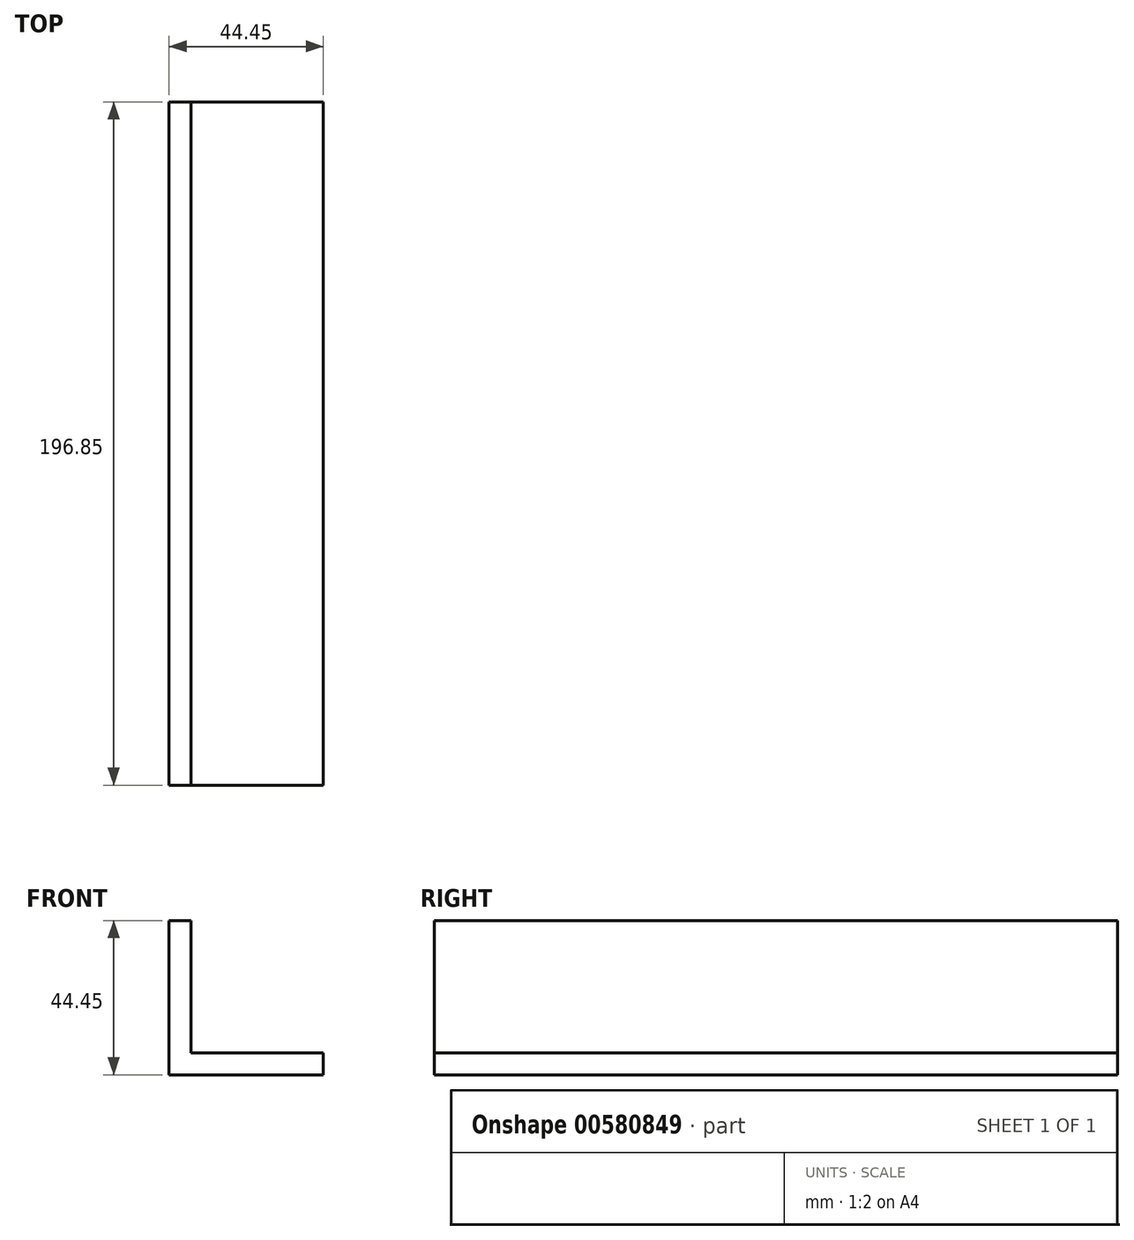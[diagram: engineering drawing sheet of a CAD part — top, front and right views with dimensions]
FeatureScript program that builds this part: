
annotation { "Feature Type Name" : "Feature", "Feature Type Description" : "" }
export const myFeature = defineFeature(function(context is Context, id is Id, definition is map)
    precondition{}
    {
        {
            var Q0;
            Q0=qCreatedBy(makeId("Front.planeOp"),FACE);
            var sketch = newSketch(context, id + "F0", { "sketchPlane" : qUnion([Q0])});
            skLineSegment(sketch, "E0.bottom", {"start": v(-23.34, 19.35) * mm, "end": v(-16.99, 19.35) * mm});
            skLineSegment(sketch, "E0.top", {"start": v(-23.34, -25.1) * mm, "end": v(21.11, -25.1) * mm});
            skLineSegment(sketch, "E0.left", {"start": v(-23.34, 19.35) * mm, "end": v(-23.34, -25.1) * mm});
            skLineSegment(sketch, "E0.right", {"start": v(21.11, -18.75) * mm, "end": v(21.11, -25.1) * mm});
            skLineSegment(sketch, "E1.top", {"start": v(21.11, -18.75) * mm, "end": v(-16.99, -18.75) * mm});
            skLineSegment(sketch, "E1.right", {"start": v(-16.99, 19.35) * mm, "end": v(-16.99, -18.75) * mm});
            skSolve(sketch);
        }
        {
            var Q0;
            Q0 = qSketchRegion(id + "F0", true);
            extrude(context, id + "F1", {"entities" : qUnion([Q0]), "depth" : 196.85 * mm, "offsetDistance" : 25.4 * mm});
        }
    });
